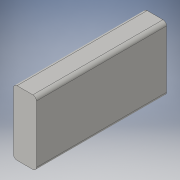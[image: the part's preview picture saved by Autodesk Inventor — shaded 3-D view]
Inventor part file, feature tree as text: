
AUTODESK INVENTOR PART (.ipt)
format: ipt  version: 2016 (Build 200138000, 138)  size: 92,672 bytes
history: native  units: in
note: dims shown in document units (in); Inventor stores cm internally (conversion verified against a paired STEP export)
features: extrude x1, fillet x1, sketch x1
ambient origin geometry x8: Origin, YZ Plane, XZ Plane, XY Plane, X Axis, Y Axis, Z Axis, Center Point
bodies: Solid1 (feature_tree)
feature tree (3):
  extrude  "Extrusion1"  Depth=1.355in
  fillet  "Fillet1"  Radius=0.482in
  sketch  "Sketch1"  dims[d0=2.729in d1=1.355in d2=0.482in d3=0.0in d4=0.075in]
